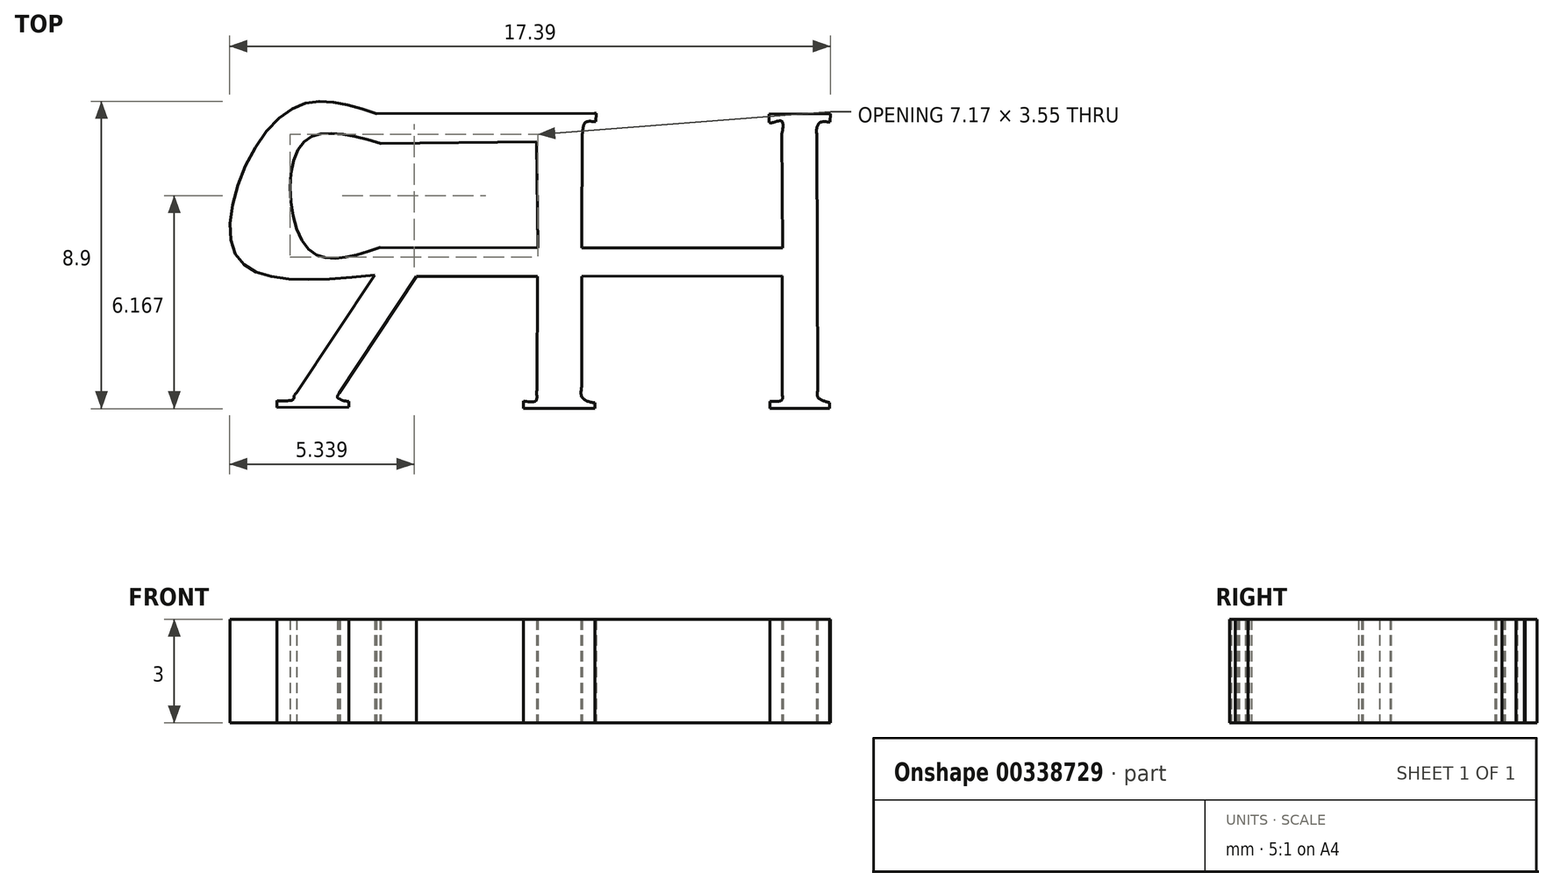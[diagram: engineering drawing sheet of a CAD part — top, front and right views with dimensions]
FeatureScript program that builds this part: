
annotation { "Feature Type Name" : "Feature", "Feature Type Description" : "" }
export const myFeature = defineFeature(function(context is Context, id is Id, definition is map)
    precondition{}
    {
        {
            var Q0;
            Q0=qCreatedBy(makeId("Top.planeOp"),FACE);
            var sketch = newSketch(context, id + "F0", { "sketchPlane" : qUnion([Q0])});
            skFitSpline(sketch, "E0", {"points": [v(-5.02, 0.4) * mm, v(-7.1, 0.36) * mm, v(-7.32, 3.36) * mm, v(-5, 3.4) * mm]});
            skLineSegment(sketch, "E1", {"start": v(-0.5, 3.45) * mm, "end": v(-0.46, 0.38) * mm});
            skLineSegment(sketch, "E2", {"start": v(-0.46, 0.38) * mm, "end": v(-5.02, 0.4) * mm});
            skLineSegment(sketch, "E3", {"start": v(-5, 3.4) * mm, "end": v(-0.5, 3.45) * mm});
            skLineSegment(sketch, "E4", {"start": v(-0.5, 3.45) * mm, "end": v(-5, 3.4) * mm});
            skFitSpline(sketch, "E5", {"points": [v(-5.12, 4.26) * mm, v(-7.78, 4.28) * mm, v(-9.24, 0.25) * mm, v(-5.18, -0.41) * mm]});
            skLineSegment(sketch, "E6", {"start": v(1.2, 4.28) * mm, "end": v(-5.12, 4.26) * mm});
            skFitSpline(sketch, "E7", {"points": [v(-7.44, -3.81) * mm, v(-7.51, -3.9) * mm, v(-7.54, -4) * mm, v(-8.01, -4.05) * mm]});
            skLineSegment(sketch, "E8", {"start": v(-5.18, -0.41) * mm, "end": v(-7.44, -3.81) * mm});
            skFitSpline(sketch, "E9", {"points": [v(-5.93, -4.07) * mm, v(-6.06, -4.05) * mm, v(-6.14, -4.03) * mm, v(-6.18, -4) * mm]});
            skFitSpline(sketch, "E10", {"points": [v(-6.18, -4) * mm, v(-6.25, -3.96) * mm, v(-6.25, -3.9) * mm, v(-6.2, -3.82) * mm]});
            skLineSegment(sketch, "E11", {"start": v(-8.01, -4.05) * mm, "end": v(-8.01, -4.25) * mm});
            skLineSegment(sketch, "E12", {"start": v(-8.01, -4.25) * mm, "end": v(-5.93, -4.23) * mm});
            skLineSegment(sketch, "E13", {"start": v(-5.93, -4.23) * mm, "end": v(-5.93, -4.07) * mm});
            skFitSpline(sketch, "E14", {"points": [v(-0.48, -3.7) * mm, v(-0.49, -3.86) * mm, v(-0.51, -4.05) * mm, v(-0.88, -4.06) * mm]});
            skLineSegment(sketch, "E15", {"start": v(-6.2, -3.82) * mm, "end": v(-3.97, -0.44) * mm});
            skLineSegment(sketch, "E16", {"start": v(-3.97, -0.44) * mm, "end": v(-0.47, -0.45) * mm});
            skLineSegment(sketch, "E17", {"start": v(-0.47, -0.45) * mm, "end": v(-0.48, -3.7) * mm});
            skFitSpline(sketch, "E18", {"points": [v(1.2, -4.11) * mm, v(0.95, -4.05) * mm, v(0.8, -3.91) * mm, v(0.81, -3.64) * mm]});
            skLineSegment(sketch, "E19", {"start": v(-0.88, -4.06) * mm, "end": v(-0.88, -4.28) * mm});
            skLineSegment(sketch, "E20", {"start": v(-0.88, -4.28) * mm, "end": v(1.2, -4.27) * mm});
            skLineSegment(sketch, "E21", {"start": v(1.2, -4.27) * mm, "end": v(1.2, -4.11) * mm});
            skFitSpline(sketch, "E22", {"points": [v(6.62, -3.7) * mm, v(6.62, -3.84) * mm, v(6.61, -4.02) * mm, v(6.26, -4.07) * mm]});
            skLineSegment(sketch, "E23", {"start": v(0.81, -3.64) * mm, "end": v(0.81, -0.45) * mm});
            skLineSegment(sketch, "E24", {"start": v(6.62, -0.44) * mm, "end": v(6.62, -3.7) * mm});
            skFitSpline(sketch, "E25", {"points": [v(7.99, -4.1) * mm, v(7.8, -4.04) * mm, v(7.65, -3.95) * mm, v(7.65, -3.74) * mm]});
            skLineSegment(sketch, "E26", {"start": v(6.26, -4.07) * mm, "end": v(6.26, -4.27) * mm});
            skLineSegment(sketch, "E27", {"start": v(6.26, -4.27) * mm, "end": v(7.99, -4.28) * mm});
            skLineSegment(sketch, "E28", {"start": v(7.99, -4.28) * mm, "end": v(7.99, -4.1) * mm});
            skFitSpline(sketch, "E29", {"points": [v(7.62, 3.61) * mm, v(7.62, 3.86) * mm, v(7.73, 4.01) * mm, v(8, 4.02) * mm]});
            skLineSegment(sketch, "E30", {"start": v(7.65, -3.74) * mm, "end": v(7.62, 3.61) * mm});
            skFitSpline(sketch, "E31", {"points": [v(6.24, 4) * mm, v(6.35, 4) * mm, v(6.6, 4.05) * mm, v(6.6, 3.68) * mm]});
            skLineSegment(sketch, "E32", {"start": v(8, 4.02) * mm, "end": v(8.01, 4.26) * mm});
            skLineSegment(sketch, "E33", {"start": v(8.01, 4.26) * mm, "end": v(6.23, 4.26) * mm});
            skLineSegment(sketch, "E34", {"start": v(6.23, 4.26) * mm, "end": v(6.24, 4) * mm});
            skFitSpline(sketch, "E35", {"points": [v(0.83, 3.65) * mm, v(0.86, 3.85) * mm, v(0.92, 4.01) * mm, v(1.23, 4.03) * mm]});
            skLineSegment(sketch, "E36", {"start": v(6.6, 3.68) * mm, "end": v(6.63, 0.53) * mm});
            skLineSegment(sketch, "E37", {"start": v(0.81, 0.52) * mm, "end": v(0.83, 3.65) * mm});
            skLineSegment(sketch, "E38", {"start": v(1.23, 4.03) * mm, "end": v(1.23, 4.28) * mm});
            skLineSegment(sketch, "E39", {"start": v(1.23, 4.28) * mm, "end": v(1.19, 4.28) * mm});
            skLineSegment(sketch, "E40", {"start": v(1.19, 4.28) * mm, "end": v(1.2, 4.27) * mm});
            skLineSegment(sketch, "E41", {"start": v(0.81, 0.64) * mm, "end": v(0.81, 0.64) * mm});
            skLineSegment(sketch, "E42", {"start": v(0.81, -0.45) * mm, "end": v(6.62, -0.44) * mm});
            skLineSegment(sketch, "E43", {"start": v(0.81, 0.38) * mm, "end": v(6.63, 0.38) * mm});
            skLineSegment(sketch, "E44", {"start": v(6.63, 0.53) * mm, "end": v(6.63, 0.38) * mm});
            skLineSegment(sketch, "E45", {"start": v(0.81, 0.64) * mm, "end": v(0.81, 0.38) * mm});
            skPoint(sketch, "E46", {"position": v(-7.13, -4.24) * mm});
            skPoint(sketch, "E47", {"position": v(7.3, -4.27) * mm});
            skSolve(sketch);
        }
        {
            var Q0;
            Q0=qSketchRegion(id+"F0",true);
            extrude(context, id + "F1", {"entities" : qUnion([Q0]), "depth" : 3 * mm});
        }
    });
